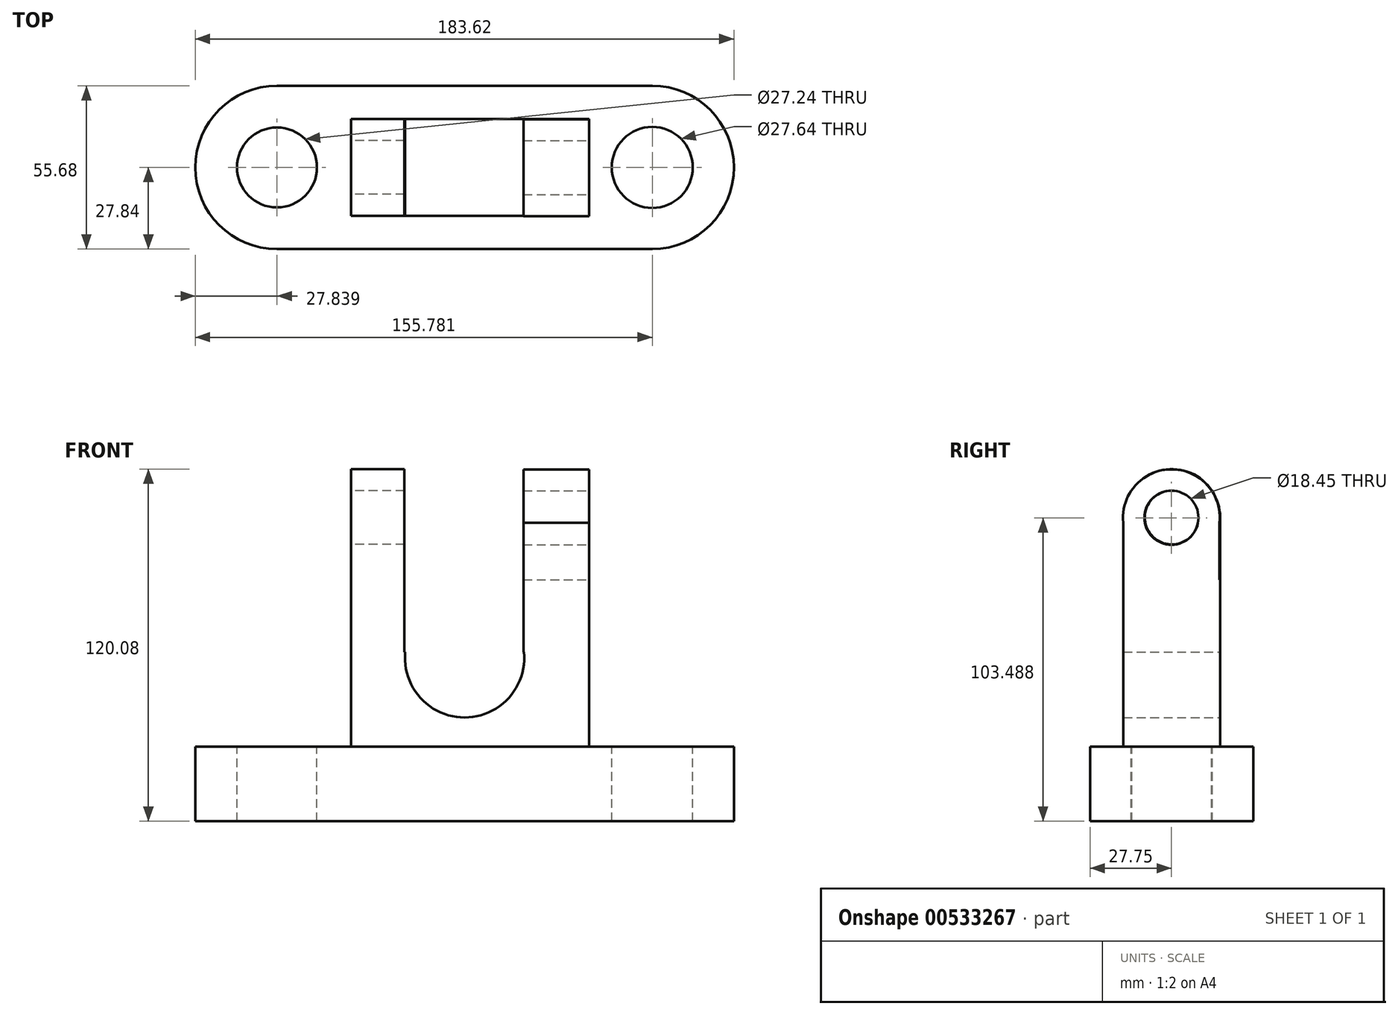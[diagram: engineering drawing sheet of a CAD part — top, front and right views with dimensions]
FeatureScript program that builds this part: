
annotation { "Feature Type Name" : "Feature", "Feature Type Description" : "" }
export const myFeature = defineFeature(function(context is Context, id is Id, definition is map)
    precondition{}
    {
        {
            var Q0;
            Q0=qCreatedBy(makeId("Top.planeOp"),FACE);
            var sketch = newSketch(context, id + "F0", { "sketchPlane" : qUnion([Q0])});
            skLineSegment(sketch, "E0.bottom", {"start": v(63.97, -27.84) * mm, "end": v(-63.97, -27.84) * mm});
            skLineSegment(sketch, "E0.top", {"start": v(63.97, 27.84) * mm, "end": v(-63.97, 27.84) * mm});
            skPoint(sketch, "E0.middle", {"position": v(0, 0) * mm});
            skArc(sketch, "E1", {"start": v(63.97, -27.84) * mm, "mid": v(91.8, 0) * mm, "end": v(63.97, 27.84) * mm});
            skArc(sketch, "E2", {"start": v(-63.97, 27.84) * mm, "mid": v(-91.8, 0) * mm, "end": v(-63.97, -27.84) * mm});
            skCircle(sketch, "E3", {"center": v(-63.97, 0) * mm, "radius": 13.62 * mm});
            skCircle(sketch, "E4", {"center": v(63.97, 0) * mm, "radius": 13.82 * mm});
            skSolve(sketch);
        }
        {
            var Q0;
            Q0=makeQuery(id+"F0.imprint","IMPRINT",FACE,{"disambiguationData":[TD([[makeQuery(id+"F0.imprint","IMPRINT",EDGE,{"derivedFrom":sQuery(id+"F0.wireOp",EDGE,"E0.bottom")}),-1.0]])]});
            extrude(context, id + "F1", {"entities" : qUnion([Q0]), "oppositeDirection" : true, "depth" : 25.4 * mm, "offsetDistance" : 25.4 * mm});
        }
        {
            var Q0;
            Q0=qCreatedBy(makeId("Front.planeOp"),FACE);
            var sketch = newSketch(context, id + "F2", { "sketchPlane" : qUnion([Q0])});
            skLineSegment(sketch, "E5.bottom", {"start": v(-38.78, 0) * mm, "end": v(42.38, 0) * mm});
            skLineSegment(sketch, "E5.top", {"start": v(-38.78, 32.3) * mm, "end": v(-20.25, 32.3) * mm});
            skLineSegment(sketch, "E5.left", {"start": v(-38.78, 0) * mm, "end": v(-38.78, 32.3) * mm});
            skLineSegment(sketch, "E5.right", {"start": v(42.38, 0) * mm, "end": v(42.38, 32.3) * mm});
            skArc(sketch, "E6", {"start": v(-20.25, 32.3) * mm, "mid": v(0, 10) * mm, "end": v(20.25, 32.3) * mm});
            skLineSegment(sketch, "E7.trimOffspring", {"start": v(20.25, 32.3) * mm, "end": v(42.38, 32.3) * mm});
            skSolve(sketch);
        }
        {
            var Q0;
            Q0=makeQuery(id+"F2.imprint","IMPRINT",FACE,{"disambiguationData":[TD([[makeQuery(id+"F2.imprint","IMPRINT",EDGE,{"derivedFrom":sQuery(id+"F2.wireOp",EDGE,"TuTYFKTE-ahRu-Bwgc-yjjx-OWpL11QLIWcn.bottom")}),1.0]])]});
            var Q1;
            Q1=makeQuery(id+"F2.imprint","IMPRINT",FACE,{"disambiguationData":[TD([[makeQuery(id+"F2.imprint","IMPRINT",EDGE,{"derivedFrom":sQuery(id+"F2.wireOp",EDGE,"TuTYFKTE-ahRu-Bwgc-yjjx-OWpL11QLIWcn.top")}),-1.0]])]});
            var Q2;
            Q2=makeQuery(id+"F2.imprint","IMPRINT",FACE,{"disambiguationData":[TD([[makeQuery(id+"F2.imprint","IMPRINT",EDGE,{"derivedFrom":sQuery(id+"F2.wireOp",EDGE,"E5.bottom")}),1.0]])]});
            extrude(context, id + "F3", {"entities" : qUnion([Q0, Q1, Q2]), "endBound" : BoundingType.SYMMETRIC, "depth" : 33.02 * mm, "offsetDistance" : 25.4 * mm});
        }
        {
            var Q0;
            Q0=makeQuery(id+"F3.opExtrude","SWEPT_FACE",FACE,{"disambiguationData":[OSD([sQuery(id+"F2.wireOp",EDGE,"E5.left")])]});
            var sketch = newSketch(context, id + "F4", { "sketchPlane" : qUnion([Q0])});
            skLineSegment(sketch, "E8.left", {"start": v(-16.51, 56.97) * mm, "end": v(-16.51, 56.97) * mm});
            skLineSegment(sketch, "E8.right", {"start": v(16.5, 56.97) * mm, "end": v(16.5, 56.97) * mm});
            skLineSegment(sketch, "E9.left", {"start": v(-16.51, 56.97) * mm, "end": v(-16.51, 78.17) * mm});
            skLineSegment(sketch, "E9.right", {"start": v(16.51, 56.97) * mm, "end": v(16.51, 78.17) * mm});
            skArc(sketch, "E10", {"start": v(16.5, 78.17) * mm, "mid": v(0, 94.68) * mm, "end": v(-16.51, 78.17) * mm});
            skCircle(sketch, "E11", {"center": v(0, 78.17) * mm, "radius": 9.15 * mm});
            skLineSegment(sketch, "E12.bottom", {"start": v(-16.51, 32.3) * mm, "end": v(-16.51, 32.3) * mm});
            skLineSegment(sketch, "E12.left", {"start": v(-16.51, 32.3) * mm, "end": v(-16.51, 56.97) * mm});
            skLineSegment(sketch, "E12.right", {"start": v(-16.51, 32.3) * mm, "end": v(-16.51, 56.97) * mm});
            skLineSegment(sketch, "E13.bottom", {"start": v(16.51, 56.97) * mm, "end": v(16.51, 56.97) * mm});
            skLineSegment(sketch, "E13.top", {"start": v(16.51, 32.3) * mm, "end": v(16.51, 32.3) * mm});
            skLineSegment(sketch, "E13.left", {"start": v(16.51, 56.97) * mm, "end": v(16.51, 32.3) * mm});
            skLineSegment(sketch, "E13.right", {"start": v(16.51, 56.97) * mm, "end": v(16.51, 32.3) * mm});
            skSolve(sketch);
        }
        {
            var Q0;
            Q0=makeQuery(id+"F4.imprint","IMPRINT",FACE,{"disambiguationData":[TD([[makeQuery(id+"F4.imprint","IMPRINT",EDGE,{"derivedFrom":sQuery(id+"F4.wireOp",EDGE,"E9.left")}),-1.0]])]});
            extrude(context, id + "F5", {"entities" : qUnion([Q0]), "operationType" : NewBodyOperationType.ADD, "oppositeDirection" : true, "depth" : 18.29 * mm, "offsetDistance" : 25.4 * mm});
        }
        {
            var Q0;
            Q0=makeQuery(id+"F3.opExtrude","SWEPT_FACE",FACE,{"disambiguationData":[OSD([sQuery(id+"F2.wireOp",EDGE,"E5.right")])]});
            var sketch = newSketch(context, id + "F6", { "sketchPlane" : qUnion([Q0])});
            skLineSegment(sketch, "E14.left", {"start": v(-16.51, 56.97) * mm, "end": v(-16.51, 56.97) * mm});
            skLineSegment(sketch, "E14.right", {"start": v(16.5, 56.97) * mm, "end": v(16.5, 56.97) * mm});
            skLineSegment(sketch, "E15.left", {"start": v(-16.51, 56.97) * mm, "end": v(-16.51, 76.42) * mm});
            skLineSegment(sketch, "E15.right", {"start": v(16.33, 56.97) * mm, "end": v(16.33, 76.42) * mm});
            skArc(sketch, "E16", {"start": v(16.33, 76.42) * mm, "mid": v(-0.1, 94.6) * mm, "end": v(-16.5, 76.42) * mm});
            skCircle(sketch, "E17", {"center": v(-0.1, 78.09) * mm, "radius": 9.22 * mm});
            skLineSegment(sketch, "E18.bottom", {"start": v(16.33, 56.97) * mm, "end": v(16.51, 56.97) * mm});
            skLineSegment(sketch, "E18.top", {"start": v(-16.51, 32.3) * mm, "end": v(16.51, 32.3) * mm});
            skLineSegment(sketch, "E18.left", {"start": v(-16.51, 56.97) * mm, "end": v(-16.51, 32.3) * mm});
            skLineSegment(sketch, "E18.right", {"start": v(16.51, 56.97) * mm, "end": v(16.51, 32.3) * mm});
            skSolve(sketch);
        }
        {
            var Q0;
            Q0=makeQuery(id+"F6.imprint","IMPRINT",FACE,{"disambiguationData":[TD([[makeQuery(id+"F6.imprint","IMPRINT",EDGE,{"derivedFrom":sQuery(id+"F6.wireOp",EDGE,"E15.left")}),-1.0]])]});
            extrude(context, id + "F7", {"entities" : qUnion([Q0]), "operationType" : NewBodyOperationType.ADD, "oppositeDirection" : true, "depth" : 22.35 * mm, "offsetDistance" : 25.4 * mm});
        }
    });
